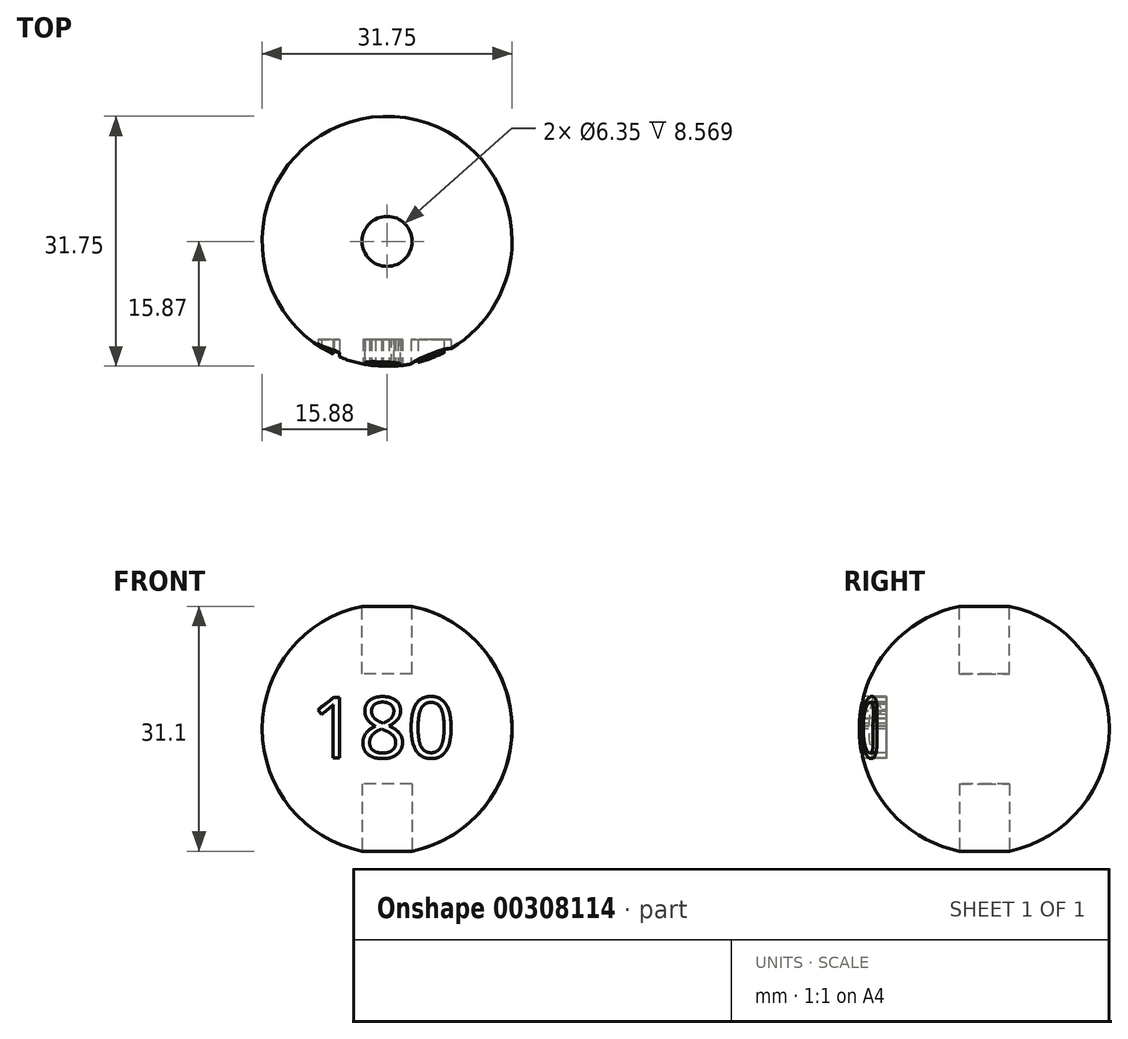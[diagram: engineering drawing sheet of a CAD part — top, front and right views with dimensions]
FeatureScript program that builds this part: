
annotation { "Feature Type Name" : "Feature", "Feature Type Description" : "" }
export const myFeature = defineFeature(function(context is Context, id is Id, definition is map)
    precondition{}
    {
        {
            var Q0;
            Q0=qCreatedBy(makeId("Front.planeOp"),FACE);
            var sketch = newSketch(context, id + "F0", { "sketchPlane" : qUnion([Q0])});
            skArc(sketch, "E0", {"start": v(0, 15.88) * mm, "mid": v(-15.88, 0) * mm, "end": v(0, -15.88) * mm});
            skLineSegment(sketch, "E1", {"start": v(0, 15.88) * mm, "end": v(0, -15.88) * mm});
            skSolve(sketch);
        }
        {
            var Q0;
            Q0=qCreatedBy(makeId("Top.planeOp"),FACE);
            var sketch = newSketch(context, id + "F1", { "sketchPlane" : qUnion([Q0])});
            skCircle(sketch, "E2", {"center": v(0, 0) * mm, "radius": 15.88 * mm});
            skSolve(sketch);
        }
        {
            var Q0;
            Q0=makeQuery(id+"F0.imprint","IMPRINT",FACE,{"disambiguationData":[TD([[makeQuery(id+"F0.imprint","IMPRINT",EDGE,{"derivedFrom":sQuery(id+"F0.wireOp",EDGE,"E0")}),1.0]])]});
            var Q1;
            Q1=sQuery(id+"F1.wireOp",EDGE,"E2");
            revolve(context, id + "F2", {"entities" : qUnion([Q0]), "axis" : qUnion([Q1]), "revolveType" : RevolveType.FULL});
        }
        {
            var Q0;
            Q0=qCreatedBy(makeId("Top.planeOp"),FACE);
            cPlane(context, id + "F3", {"entities" : qUnion([Q0]), "cplaneType" : CPlaneType.OFFSET, "offset" : 16.5 * mm, "width" : 152.4 * mm, "height" : 152.4 * mm});
        }
        {
            var Q0;
            Q0=qCreatedBy(id+"F3.planeOp",FACE);
            var sketch = newSketch(context, id + "F4", { "sketchPlane" : qUnion([Q0])});
            skCircle(sketch, "E3", {"center": v(0, 0) * mm, "radius": 3.18 * mm});
            skSolve(sketch);
        }
        {
            var Q0;
            Q0=makeQuery(id+"F4.imprint","IMPRINT",FACE,{"disambiguationData":[TD([[makeQuery(id+"F4.imprint","IMPRINT",EDGE,{"derivedFrom":sQuery(id+"F4.wireOp",EDGE,"E3")}),1.0]])]});
            extrude(context, id + "F5", {"entities" : qUnion([Q0]), "operationType" : NewBodyOperationType.REMOVE, "oppositeDirection" : true, "depth" : 9.52 * mm});
        }
        {
            var Q0;
            Q0=qCreatedBy(makeId("Top.planeOp"),FACE);
            cPlane(context, id + "F6", {"entities" : qUnion([Q0]), "cplaneType" : CPlaneType.OFFSET, "offset" : 16.5 * mm, "oppositeDirection" : true, "width" : 152.4 * mm, "height" : 152.4 * mm});
        }
        {
            var Q0;
            Q0=qCreatedBy(id+"F6.planeOp",FACE);
            var sketch = newSketch(context, id + "F7", { "sketchPlane" : qUnion([Q0])});
            skCircle(sketch, "E4", {"center": v(0, 0) * mm, "radius": 3.18 * mm});
            skSolve(sketch);
        }
        {
            var Q0;
            Q0 = qSketchRegion(id + "F7", true);
            extrude(context, id + "F8", {"entities" : qUnion([Q0]), "operationType" : NewBodyOperationType.REMOVE, "depth" : 9.52 * mm});
        }
        {
            var Q0;
            Q0=qCreatedBy(makeId("Front.planeOp"),FACE);
            cPlane(context, id + "F9", {"entities" : qUnion([Q0]), "cplaneType" : CPlaneType.OFFSET, "offset" : 16.5 * mm, "width" : 152.4 * mm, "height" : 152.4 * mm});
        }
        {
            var Q0;
            Q0=qCreatedBy(id+"F9.planeOp",FACE);
            var sketch = newSketch(context, id + "F10", { "sketchPlane" : qUnion([Q0])});
            skText(sketch, "E5", { "text": "180", "fontName": "OpenSans-Regular.ttf"});
            const initialGuessF10  = {"E5": [-0.00977, -0.00369, 1, 0, 0.00774]};
            skSetInitialGuess(sketch, initialGuessF10);
            skSolve(sketch);
        }
        {
            var Q0;
            Q0 = qSketchRegion(id + "F10", true);
            extrude(context, id + "F11", {"entities" : qUnion([Q0]), "operationType" : NewBodyOperationType.REMOVE, "oppositeDirection" : true, "depth" : 4.06 * mm});
        }
    });
